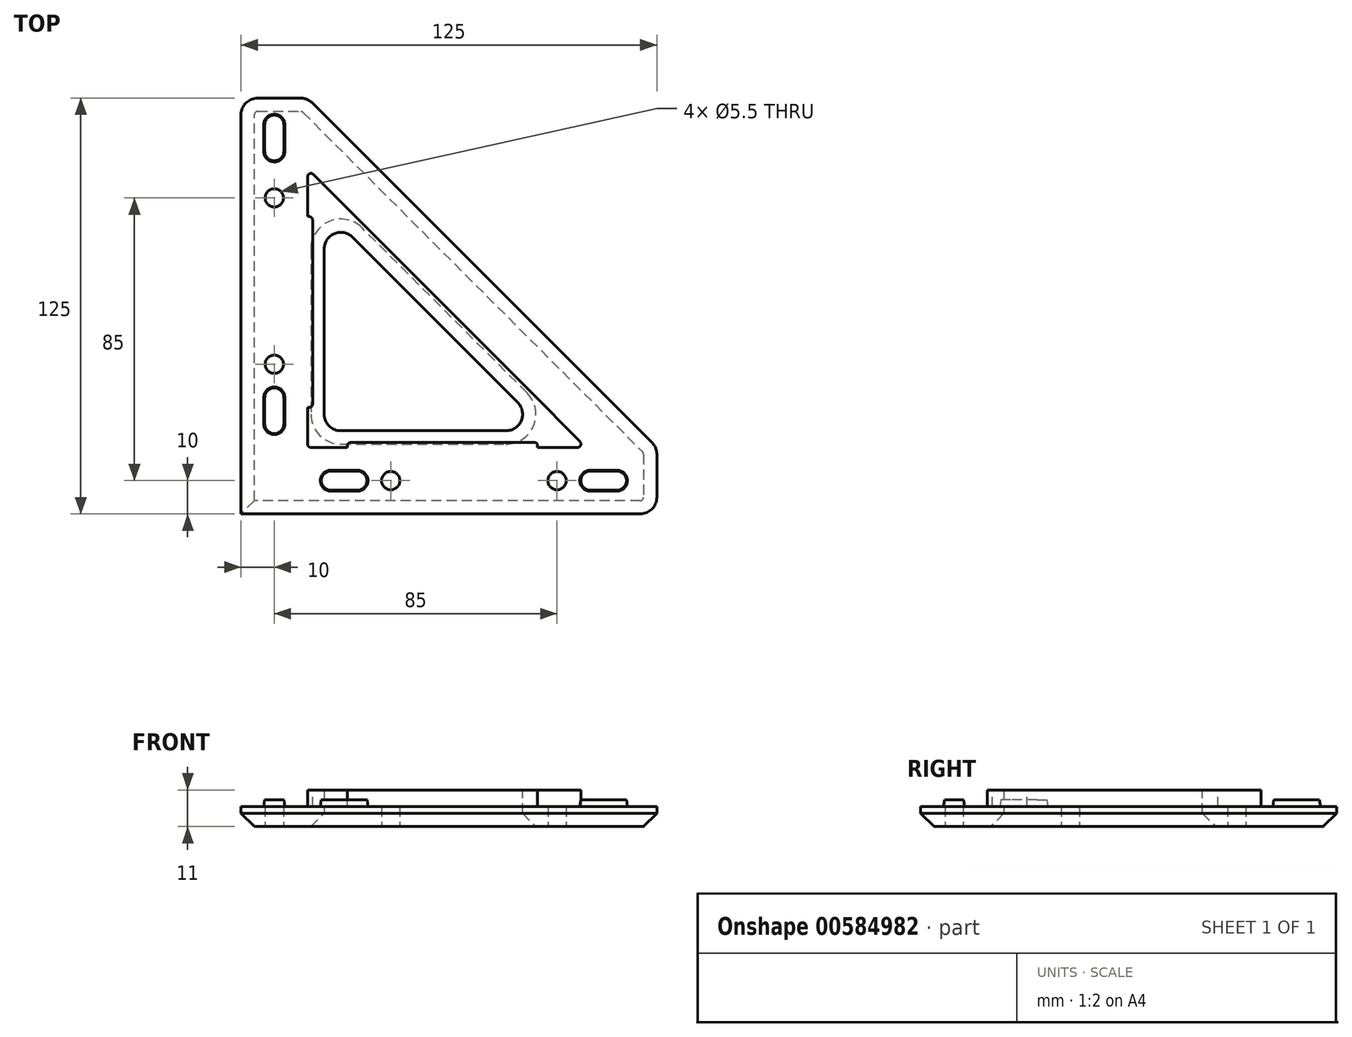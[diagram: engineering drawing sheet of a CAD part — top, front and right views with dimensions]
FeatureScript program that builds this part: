
annotation { "Feature Type Name" : "Feature", "Feature Type Description" : "" }
export const myFeature = defineFeature(function(context is Context, id is Id, definition is map)
    precondition{}
    {
        {
            var Q0;
            Q0=qCreatedBy(makeId("Top.planeOp"),FACE);
            var sketch = newSketch(context, id + "F0", { "sketchPlane" : qUnion([Q0])});
            skLineSegment(sketch, "E0", {"start": v(0, 0) * mm, "end": v(0, 129.04) * mm, "construction": true});
            skLineSegment(sketch, "E1", {"start": v(0, 0) * mm, "end": v(140.06, 0) * mm, "construction": true});
            skLineSegment(sketch, "E2", {"start": v(0, 125) * mm, "end": v(0, 0) * mm});
            skLineSegment(sketch, "E3", {"start": v(125, 0) * mm, "end": v(125, 20) * mm});
            skLineSegment(sketch, "E4", {"start": v(125, 20) * mm, "end": v(20, 125) * mm});
            skLineSegment(sketch, "E5", {"start": v(20, 125) * mm, "end": v(0, 125) * mm});
            skLineSegment(sketch, "E6", {"start": v(25, 91.72) * mm, "end": v(91.72, 25) * mm});
            skLineSegment(sketch, "E7", {"start": v(91.72, 25) * mm, "end": v(25, 25) * mm});
            skLineSegment(sketch, "E8", {"start": v(25, 25) * mm, "end": v(25, 91.72) * mm});
            skLineSegment(sketch, "E9", {"start": v(0, 0) * mm, "end": v(125, 0) * mm});
            skSolve(sketch);
        }
        {
            var Q0;
            Q0=makeQuery(id+"F0.imprint","IMPRINT",FACE,{"disambiguationData":[TD([[makeQuery(id+"F0.imprint","IMPRINT",EDGE,{"derivedFrom":sQuery(id+"F0.wireOp",EDGE,"E2")}),1.0]])]});
            extrude(context, id + "F1", {"entities" : qUnion([Q0]), "depth" : 6 * mm, "offsetDistance" : 25 * mm});
        }
        {
            var Q0;
            Q0=makeQuery(id+"F1.opExtrude","SWEPT_EDGE",EDGE,{"disambiguationData":[OSD([sQuery(id+"F0.wireOp",EDGE,"E6"),sQuery(id+"F0.wireOp",EDGE,"E8")])]});
            var Q1;
            Q1=makeQuery(id+"F1.opExtrude","SWEPT_EDGE",EDGE,{"disambiguationData":[OSD([sQuery(id+"F0.wireOp",EDGE,"E6"),sQuery(id+"F0.wireOp",EDGE,"E7")])]});
            var Q2;
            Q2=makeQuery(id+"F1.opExtrude","SWEPT_EDGE",EDGE,{"disambiguationData":[OSD([sQuery(id+"F0.wireOp",EDGE,"E7"),sQuery(id+"F0.wireOp",EDGE,"E8")])]});
            var Q3;
            Q3=makeQuery(id+"F1.opExtrude","SWEPT_EDGE",EDGE,{"disambiguationData":[OSD([sQuery(id+"F0.wireOp",EDGE,"E2"),sQuery(id+"F0.wireOp",EDGE,"E5")])]});
            var Q4;
            Q4=makeQuery(id+"F1.opExtrude","SWEPT_EDGE",EDGE,{"disambiguationData":[OSD([sQuery(id+"F0.wireOp",EDGE,"E4"),sQuery(id+"F0.wireOp",EDGE,"E5")])]});
            var Q5;
            Q5=makeQuery(id+"F1.opExtrude","SWEPT_EDGE",EDGE,{"disambiguationData":[OSD([sQuery(id+"F0.wireOp",EDGE,"E3"),sQuery(id+"F0.wireOp",EDGE,"E4")])]});
            var Q6;
            Q6=makeQuery(id+"F1.opExtrude","SWEPT_EDGE",EDGE,{"disambiguationData":[OSD([sQuery(id+"F0.wireOp",EDGE,"E3"),sQuery(id+"F0.wireOp",EDGE,"E9")])]});
            fillet(context, id + "F2", {"entities" : qUnion([Q0, Q1, Q2, Q3, Q4, Q5, Q6]), "radius" : 5 * mm, "tangentPropagation" : true, "allowEdgeOverflow" : false});
        }
        {
            var Q0;
            Q0=makeQuery(id+"F1.opExtrude","CAP_FACE",FACE,{"disambiguationData":[OSD([sQuery(id+"F0.wireOp",EDGE,"E2"),sQuery(id+"F0.wireOp",EDGE,"E3"),sQuery(id+"F0.wireOp",EDGE,"E4"),sQuery(id+"F0.wireOp",EDGE,"E5"),sQuery(id+"F0.wireOp",EDGE,"E6"),sQuery(id+"F0.wireOp",EDGE,"E7"),sQuery(id+"F0.wireOp",EDGE,"E8"),sQuery(id+"F0.wireOp",EDGE,"E9")])],"isStart":false});
            var sketch = newSketch(context, id + "F3", { "sketchPlane" : qUnion([Q0])});
            skLineSegment(sketch, "E10.0", {"start": v(25, 30) * mm, "end": v(25, 79.64) * mm});
            skArc(sketch, "E11.0", {"start": v(25, 79.64) * mm, "mid": v(28.09, 84.26) * mm, "end": v(33.54, 83.18) * mm});
            skLineSegment(sketch, "E12.0", {"start": v(33.54, 83.18) * mm, "end": v(83.18, 33.54) * mm});
            skArc(sketch, "E13.0", {"start": v(83.18, 33.54) * mm, "mid": v(84.26, 28.09) * mm, "end": v(79.64, 25) * mm});
            skLineSegment(sketch, "E14.0", {"start": v(79.64, 25) * mm, "end": v(30, 25) * mm});
            skArc(sketch, "E15.0", {"start": v(30, 25) * mm, "mid": v(26.46, 26.46) * mm, "end": v(25, 30) * mm});
            skLineSegment(sketch, "E16.2", {"start": v(37.07, 86.72) * mm, "end": v(86.72, 37.07) * mm});
            skLineSegment(sketch, "E16.3", {"start": v(20, 30) * mm, "end": v(20, 79.64) * mm});
            skLineSegment(sketch, "E16.5", {"start": v(79.64, 20) * mm, "end": v(30, 20) * mm});
            skLineSegment(sketch, "E17", {"start": v(20, 30) * mm, "end": v(20, 20) * mm});
            skLineSegment(sketch, "E18", {"start": v(20, 20) * mm, "end": v(30, 20) * mm});
            skLineSegment(sketch, "E19", {"start": v(86.72, 37.07) * mm, "end": v(103.57, 20) * mm});
            skLineSegment(sketch, "E20", {"start": v(103.57, 20) * mm, "end": v(79.64, 20) * mm});
            skLineSegment(sketch, "E21", {"start": v(20, 79.64) * mm, "end": v(20, 103.79) * mm});
            skLineSegment(sketch, "E22", {"start": v(20, 103.79) * mm, "end": v(37.07, 86.72) * mm});
            skSolve(sketch);
        }
        {
            var Q0;
            Q0=makeQuery(id+"F3.imprint","IMPRINT",FACE,{"disambiguationData":[TD([[makeQuery(id+"F3.imprint","IMPRINT",EDGE,{"derivedFrom":sQuery(id+"F3.wireOp",EDGE,"E10.0")}),1.0]])]});
            extrude(context, id + "F4", {"entities" : qUnion([Q0]), "operationType" : NewBodyOperationType.ADD, "depth" : 5 * mm, "offsetDistance" : 25 * mm});
        }
        {
            var Q0;
            Q0=makeQuery(id+"F1.opExtrude","CAP_EDGE",EDGE,{"disambiguationData":[OSD([sQuery(id+"F0.wireOp",EDGE,"E6")])],"isStart":true});
            var Q1;
            Q1=makeQuery(id+"F1.opExtrude","CAP_EDGE",EDGE,{"disambiguationData":[OSD([sQuery(id+"F0.wireOp",EDGE,"E4")])],"isStart":true});
            chamfer(context, id + "F5", {"entities" : qUnion([Q0, Q1]), "width" : 4 * mm, "tangentPropagation" : true});
        }
        {
            var Q0;
            Q0=makeQuery(id+"F4.opExtrude","SWEPT_EDGE",EDGE,{"disambiguationData":[OSD([sQuery(id+"F3.wireOp",EDGE,"E21"),sQuery(id+"F3.wireOp",EDGE,"E22")])]});
            var Q1;
            Q1=makeQuery(id+"F4.opExtrude","SWEPT_EDGE",EDGE,{"disambiguationData":[OSD([sQuery(id+"F3.wireOp",EDGE,"E17"),sQuery(id+"F3.wireOp",EDGE,"E18")])]});
            var Q2;
            Q2=makeQuery(id+"F4.opExtrude","SWEPT_EDGE",EDGE,{"disambiguationData":[OSD([sQuery(id+"F3.wireOp",EDGE,"E19"),sQuery(id+"F3.wireOp",EDGE,"E20")])]});
            fillet(context, id + "F6", {"entities" : qUnion([Q0, Q1, Q2]), "radius" : 1 * mm, "tangentPropagation" : true, "allowEdgeOverflow" : false});
        }
        {
            var Q0;
            Q0=makeQuery(id+"F1.opExtrude","CAP_FACE",FACE,{"disambiguationData":[OSD([sQuery(id+"F0.wireOp",EDGE,"E2"),sQuery(id+"F0.wireOp",EDGE,"E3"),sQuery(id+"F0.wireOp",EDGE,"E4"),sQuery(id+"F0.wireOp",EDGE,"E5"),sQuery(id+"F0.wireOp",EDGE,"E6"),sQuery(id+"F0.wireOp",EDGE,"E7"),sQuery(id+"F0.wireOp",EDGE,"E8"),sQuery(id+"F0.wireOp",EDGE,"E9")])],"isStart":true});
            var sketch = newSketch(context, id + "F7", { "sketchPlane" : qUnion([Q0])});
            skLineSegment(sketch, "E23", {"start": v(121, -10) * mm, "end": v(2.2, -10) * mm, "construction": true});
            skLineSegment(sketch, "E24", {"start": v(10, -121) * mm, "end": v(10, -10) * mm, "construction": true});
            skPoint(sketch, "E25", {"position": v(95, -10) * mm});
            skPoint(sketch, "E26", {"position": v(45, -10) * mm});
            skPoint(sketch, "E27", {"position": v(10, -45) * mm});
            skPoint(sketch, "E28", {"position": v(10, -95) * mm});
            skArc(sketch, "E29", {"start": v(6.85, -118) * mm, "mid": v(10, -121.15) * mm, "end": v(13.15, -118) * mm});
            skLineSegment(sketch, "E30", {"start": v(163.84, 190.14) * mm, "end": v(45.04, 190.14) * mm, "construction": true});
            skLineSegment(sketch, "E31", {"start": v(52.84, 79.14) * mm, "end": v(52.84, 190.14) * mm, "construction": true});
            skPoint(sketch, "E32", {"position": v(142.84, 190.14) * mm});
            skPoint(sketch, "E33", {"position": v(82.84, 190.14) * mm});
            skPoint(sketch, "E34", {"position": v(52.84, 160.14) * mm});
            skPoint(sketch, "E35", {"position": v(52.84, 100.14) * mm});
            skCircle(sketch, "E36", {"center": v(52.84, 83.34) * mm, "radius": 3.15 * mm});
            skLineSegment(sketch, "E37", {"start": v(16.48, -113) * mm, "end": v(-1.93, -113) * mm, "construction": true});
            skArc(sketch, "E38.MirrorC", {"start": v(6.85, -108) * mm, "mid": v(10, -104.85) * mm, "end": v(13.15, -108) * mm});
            skLineSegment(sketch, "E39", {"start": v(13.15, -118) * mm, "end": v(13.15, -108) * mm});
            skLineSegment(sketch, "E40", {"start": v(6.85, -118) * mm, "end": v(6.85, -108) * mm});
            skSolve(sketch);
        }
        {
            var Q0;
            Q0=sQuery(id+"F7.wireOp",VERTEX,"E25");
            var Q1;
            Q1=sQuery(id+"F7.wireOp",VERTEX,"E26");
            var Q2;
            Q2=sQuery(id+"F7.wireOp",VERTEX,"E27");
            var Q3;
            Q3=sQuery(id+"F7.wireOp",VERTEX,"E28");
            var Q4;
            Q4=makeQuery(id+"F1.opExtrude","SWEPT_BODY",BODY,{"disambiguationData":[OSD([sQuery(id+"F0.wireOp",EDGE,"E2"),sQuery(id+"F0.wireOp",EDGE,"E3"),sQuery(id+"F0.wireOp",EDGE,"E4"),sQuery(id+"F0.wireOp",EDGE,"E5"),sQuery(id+"F0.wireOp",EDGE,"E6"),sQuery(id+"F0.wireOp",EDGE,"E7"),sQuery(id+"F0.wireOp",EDGE,"E8"),sQuery(id+"F0.wireOp",EDGE,"E9")])]});
            hole(context, id + "F8", {"style" : HoleStyle.SIMPLE, "endStyle" : HoleEndStyle.THROUGH, "standardTappedOrClearance" : lookupTablePath({ "standard" : "ISO", "fit" : "Normal", "size" : "M5", "type" : "Clearance" }), "standardBlindInLast" : lookupTablePath({ "fit" : "Standard", "standard" : "ISO", "size" : "M5", "type" : "Clearance" }), "holeDiameter" : 5.5 * mm, "majorDiameter" : 5 * mm, "isTappedThrough" : true, "tappedDepth" : 12 * mm, "tapClearance" : 3, "startFromSketch" : true, "locations" : qUnion([Q0, Q1, Q2, Q3]), "scope" : qUnion([Q4])});
        }
        {
            var Q0;
            Q0=makeQuery(id+"F4.opExtrude","CAP_FACE",FACE,{"disambiguationData":[OSD([sQuery(id+"F3.wireOp",EDGE,"E10.0"),sQuery(id+"F3.wireOp",EDGE,"E11.0"),sQuery(id+"F3.wireOp",EDGE,"E12.0"),sQuery(id+"F3.wireOp",EDGE,"E13.0"),sQuery(id+"F3.wireOp",EDGE,"E14.0"),sQuery(id+"F3.wireOp",EDGE,"E15.0"),sQuery(id+"F3.wireOp",EDGE,"E16.2"),sQuery(id+"F3.wireOp",EDGE,"E16.3"),sQuery(id+"F3.wireOp",EDGE,"E16.5"),sQuery(id+"F3.wireOp",EDGE,"E17"),sQuery(id+"F3.wireOp",EDGE,"E18"),sQuery(id+"F3.wireOp",EDGE,"E19"),sQuery(id+"F3.wireOp",EDGE,"E20"),sQuery(id+"F3.wireOp",EDGE,"E21"),sQuery(id+"F3.wireOp",EDGE,"E22")])],"isStart":false});
            var sketch = newSketch(context, id + "F9", { "sketchPlane" : qUnion([Q0])});
            skLineSegment(sketch, "E41.0", {"start": v(32, 20) * mm, "end": v(89.17, 20) * mm});
            skLineSegment(sketch, "E42", {"start": v(32, 20) * mm, "end": v(32, 21.5) * mm});
            skLineSegment(sketch, "E43", {"start": v(32, 21.5) * mm, "end": v(89.17, 21.5) * mm});
            skLineSegment(sketch, "E44", {"start": v(89.17, 21.5) * mm, "end": v(89.17, 20) * mm});
            skPoint(sketch, "E45.orphan", {"position": v(21, 20) * mm});
            skPoint(sketch, "E46.orphan", {"position": v(101.17, 20) * mm});
            skLineSegment(sketch, "E47.0", {"start": v(20, 32) * mm, "end": v(20, 89.37) * mm});
            skLineSegment(sketch, "E48", {"start": v(21.5, 89.37) * mm, "end": v(21.5, 32) * mm});
            skLineSegment(sketch, "E49", {"start": v(20, 32) * mm, "end": v(21.5, 32) * mm});
            skLineSegment(sketch, "E50", {"start": v(20, 89.37) * mm, "end": v(21.5, 89.37) * mm});
            skPoint(sketch, "E51.orphan", {"position": v(20, 21) * mm});
            skPoint(sketch, "E52.orphan", {"position": v(20, 101.37) * mm});
            skSolve(sketch);
        }
        {
            var Q0;
            Q0 = qSketchRegion(id + "F9", true);
            var Q1;
            Q1=makeQuery(id+"F1.opExtrude","CAP_FACE",FACE,{"disambiguationData":[OSD([sQuery(id+"F0.wireOp",EDGE,"E2"),sQuery(id+"F0.wireOp",EDGE,"E3"),sQuery(id+"F0.wireOp",EDGE,"E4"),sQuery(id+"F0.wireOp",EDGE,"E5"),sQuery(id+"F0.wireOp",EDGE,"E6"),sQuery(id+"F0.wireOp",EDGE,"E7"),sQuery(id+"F0.wireOp",EDGE,"E8"),sQuery(id+"F0.wireOp",EDGE,"E9")])],"isStart":false});
            extrude(context, id + "F10", {"entities" : qUnion([Q0]), "operationType" : NewBodyOperationType.REMOVE, "endBound" : BoundingType.UP_TO_SURFACE, "oppositeDirection" : true, "depth" : 25 * mm, "endBoundEntityFace" : qUnion([Q1]), "offsetDistance" : 25 * mm});
        }
        {
            var Q0;
            Q0=makeQuery(id+"F10.boolean.opBoolean","COPY",EDGE,{"derivedFrom":makeQuery(id+"F10.opExtrude","SWEPT_EDGE",EDGE,{"disambiguationData":[OSD([sQuery(id+"F9.wireOp",EDGE,"E48"),sQuery(id+"F9.wireOp",EDGE,"E50")])]})});
            var Q1;
            Q1=makeQuery(id+"F10.boolean.opBoolean","COPY",EDGE,{"derivedFrom":makeQuery(id+"F10.opExtrude","SWEPT_EDGE",EDGE,{"disambiguationData":[OSD([sQuery(id+"F9.wireOp",EDGE,"E48"),sQuery(id+"F9.wireOp",EDGE,"E49")])]})});
            var Q2;
            Q2=makeQuery(id+"F10.boolean.opBoolean","COPY",EDGE,{"derivedFrom":makeQuery(id+"F10.opExtrude","SWEPT_EDGE",EDGE,{"disambiguationData":[OSD([sQuery(id+"F9.wireOp",EDGE,"E42"),sQuery(id+"F9.wireOp",EDGE,"E43")])]})});
            var Q3;
            Q3=makeQuery(id+"F10.boolean.opBoolean","COPY",EDGE,{"derivedFrom":makeQuery(id+"F10.opExtrude","SWEPT_EDGE",EDGE,{"disambiguationData":[OSD([sQuery(id+"F9.wireOp",EDGE,"E43"),sQuery(id+"F9.wireOp",EDGE,"E44")])]})});
            fillet(context, id + "F11", {"entities" : qUnion([Q0, Q1, Q2, Q3]), "radius" : 1 * mm, "tangentPropagation" : true, "allowEdgeOverflow" : false});
        }
        {
            var Q0;
            {var subQ0=sQuery(id+"F0.wireOp",EDGE,"E9");var subQ1=sQuery(id+"F0.wireOp",EDGE,"E8");var subQ2=sQuery(id+"F0.wireOp",EDGE,"E7");var subQ3=sQuery(id+"F0.wireOp",EDGE,"E6");var subQ4=sQuery(id+"F0.wireOp",EDGE,"E5");var subQ5=sQuery(id+"F0.wireOp",EDGE,"E4");var subQ6=sQuery(id+"F0.wireOp",EDGE,"E3");var subQ7=sQuery(id+"F0.wireOp",EDGE,"E2");Q0=makeQuery(id+"F10.boolean.opBoolean","MERGE",FACE,{"derivedFrom":[makeQuery(id+"F1.opExtrude","CAP_FACE",FACE,{"disambiguationData":[OSD([subQ7,subQ6,subQ5,subQ4,subQ3,subQ2,subQ1,subQ0])],"isStart":false}),makeQuery(id+"F10.opExtrude","CAP_FACE",FACE,{"disambiguationData":[OSD([subQ7,subQ6,subQ5,subQ4,subQ3,subQ2,subQ1,subQ0]),OD(0.0)],"isStart":false}),makeQuery(id+"F10.opExtrude","CAP_FACE",FACE,{"disambiguationData":[OSD([subQ7,subQ6,subQ5,subQ4,subQ3,subQ2,subQ1,subQ0]),OD(1.0)],"isStart":false})]});}
            var sketch = newSketch(context, id + "F12", { "sketchPlane" : qUnion([Q0])});
            skLineSegment(sketch, "E53", {"start": v(45, 10) * mm, "end": v(95, 10) * mm, "construction": true});
            skLineSegment(sketch, "E54", {"start": v(10, 45) * mm, "end": v(10, 95) * mm, "construction": true});
            skArc(sketch, "E55", {"start": v(6.85, 109) * mm, "mid": v(10, 105.85) * mm, "end": v(13.15, 109) * mm});
            skArc(sketch, "E56.MirrorC", {"start": v(6.85, 117) * mm, "mid": v(10, 120.15) * mm, "end": v(13.15, 117) * mm});
            skLineSegment(sketch, "E57", {"start": v(13.15, 109) * mm, "end": v(13.15, 117) * mm});
            skLineSegment(sketch, "E58", {"start": v(6.85, 109) * mm, "end": v(6.85, 117) * mm});
            skLineSegment(sketch, "E59", {"start": v(10, 95) * mm, "end": v(10, 129.1) * mm, "construction": true});
            skArc(sketch, "E60", {"start": v(6.85, 27) * mm, "mid": v(10, 23.85) * mm, "end": v(13.15, 27) * mm});
            skArc(sketch, "E61.MirrorC", {"start": v(6.85, 35) * mm, "mid": v(10, 38.15) * mm, "end": v(13.15, 35) * mm});
            skLineSegment(sketch, "E62", {"start": v(13.15, 27) * mm, "end": v(13.15, 35) * mm});
            skLineSegment(sketch, "E63", {"start": v(6.85, 27) * mm, "end": v(6.85, 35) * mm});
            skPoint(sketch, "E64.endSnap0", {"position": v(13.15, 31) * mm});
            skLineSegment(sketch, "E65", {"start": v(10, 45) * mm, "end": v(10, 3.84) * mm, "construction": true});
            skLineSegment(sketch, "E66", {"start": v(6.85, 113) * mm, "end": v(13.15, 113) * mm, "construction": true});
            skArc(sketch, "E67", {"start": v(27, 13.15) * mm, "mid": v(23.85, 10) * mm, "end": v(27, 6.85) * mm});
            skArc(sketch, "E68.MirrorC", {"start": v(35, 13.15) * mm, "mid": v(38.15, 10) * mm, "end": v(35, 6.85) * mm});
            skLineSegment(sketch, "E69", {"start": v(27, 6.85) * mm, "end": v(35, 6.85) * mm});
            skLineSegment(sketch, "E70", {"start": v(27, 13.15) * mm, "end": v(35, 13.15) * mm});
            skPoint(sketch, "E71.startSnap0", {"position": v(28.53, 1.5) * mm});
            skPoint(sketch, "E71.endSnap0", {"position": v(31, 6.85) * mm});
            skLineSegment(sketch, "E72", {"start": v(27, 10) * mm, "end": v(35, 10) * mm, "construction": true});
            skLineSegment(sketch, "E73", {"start": v(31, 6.85) * mm, "end": v(31, 13.15) * mm, "construction": true});
            skLineSegment(sketch, "E74", {"start": v(6.85, 31) * mm, "end": v(13.15, 31) * mm, "construction": true});
            skArc(sketch, "E75", {"start": v(105, 13.15) * mm, "mid": v(101.85, 10) * mm, "end": v(105, 6.85) * mm});
            skArc(sketch, "E76.MirrorC", {"start": v(113, 13.15) * mm, "mid": v(116.15, 10) * mm, "end": v(113, 6.85) * mm});
            skLineSegment(sketch, "E77", {"start": v(105, 6.85) * mm, "end": v(113, 6.85) * mm});
            skLineSegment(sketch, "E78", {"start": v(105, 13.15) * mm, "end": v(113, 13.15) * mm});
            skPoint(sketch, "E79.endSnap0", {"position": v(109, 6.85) * mm});
            skLineSegment(sketch, "E80", {"start": v(105, 10) * mm, "end": v(113, 10) * mm, "construction": true});
            skLineSegment(sketch, "E81", {"start": v(109, 6.85) * mm, "end": v(109, 13.15) * mm, "construction": true});
            skSolve(sketch);
        }
        {
            var Q0;
            Q0 = qSketchRegion(id + "F12", true);
            extrude(context, id + "F13", {"entities" : qUnion([Q0]), "operationType" : NewBodyOperationType.ADD, "depth" : 2 * mm, "offsetDistance" : 25 * mm, "hasDraft" : true, "draftAngle" : 8 * degree, "draftPullDirection" : true});
        }
    });
